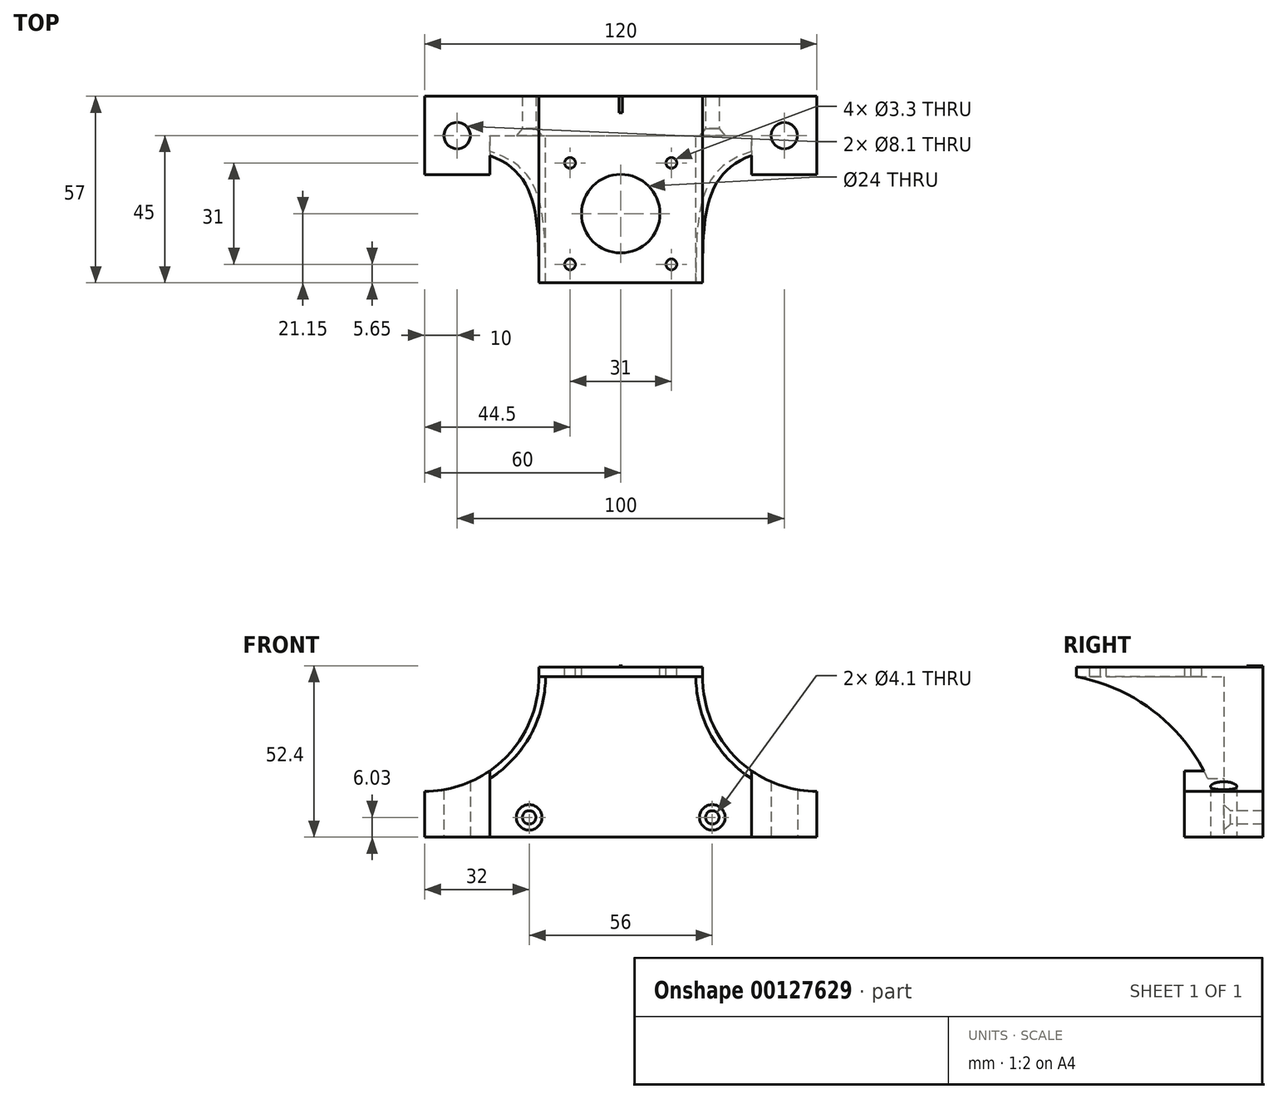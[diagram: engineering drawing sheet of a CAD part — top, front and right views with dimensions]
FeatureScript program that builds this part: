
annotation { "Feature Type Name" : "Feature", "Feature Type Description" : "" }
export const myFeature = defineFeature(function(context is Context, id is Id, definition is map)
    precondition{}
    {
        {
            var Q0;
            Q0=qCreatedBy(makeId("Front.planeOp"),FACE);
            var sketch = newSketch(context, id + "F0", { "sketchPlane" : qUnion([Q0])});
            skLineSegment(sketch, "E0.bottom", {"start": v(-27.18, 22.72) * mm, "end": v(22.82, 22.72) * mm});
            skLineSegment(sketch, "E0.top", {"start": v(-62.18, -29.28) * mm, "end": v(57.82, -29.28) * mm});
            skLineSegment(sketch, "E0.right", {"start": v(57.82, -15.28) * mm, "end": v(57.82, -29.28) * mm});
            skPoint(sketch, "E1", {"position": v(-2.18, 22.72) * mm});
            skLineSegment(sketch, "E2.top", {"start": v(-27.18, 19.72) * mm, "end": v(22.82, 19.72) * mm});
            skLineSegment(sketch, "E2.left", {"start": v(-27.18, 22.72) * mm, "end": v(-27.18, 19.72) * mm});
            skLineSegment(sketch, "E2.right", {"start": v(22.82, 22.72) * mm, "end": v(22.82, 19.72) * mm});
            skLineSegment(sketch, "E3", {"start": v(-62.18, -15.28) * mm, "end": v(57.82, -15.28) * mm, "construction": true});
            skArc(sketch, "E4", {"start": v(-62.18, -15.28) * mm, "mid": v(-37.43, -5.03) * mm, "end": v(-27.18, 19.72) * mm});
            skArc(sketch, "E5", {"start": v(22.82, 19.72) * mm, "mid": v(33.07, -5.03) * mm, "end": v(57.82, -15.28) * mm});
            skLineSegment(sketch, "E6.trimOffspring", {"start": v(-62.18, -15.28) * mm, "end": v(-62.18, -29.28) * mm});
            skPoint(sketch, "E0.left.start.orphan", {"position": v(-62.18, 22.72) * mm});
            skPoint(sketch, "E7.orphan", {"position": v(57.82, 22.72) * mm});
            skSolve(sketch);
        }
        {
            var Q0;
            Q0=makeQuery(id+"F0.imprint","IMPRINT",FACE,{"disambiguationData":[TD([[makeQuery(id+"F0.imprint","IMPRINT",EDGE,{"derivedFrom":sQuery(id+"F0.wireOp",EDGE,"E0.top")}),1.0]])]});
            var Q1;
            Q1=makeQuery(id+"F0.imprint","IMPRINT",FACE,{"disambiguationData":[TD([[makeQuery(id+"F0.imprint","IMPRINT",EDGE,{"derivedFrom":sQuery(id+"F0.wireOp",EDGE,"E0.bottom")}),-1.0]])]});
            extrude(context, id + "F1", {"entities" : qUnion([Q0, Q1]), "depth" : 12 * mm});
        }
        {
            var Q0;
            Q0=makeQuery(id+"F1.opExtrude","CAP_FACE",FACE,{"disambiguationData":[OSD([sQuery(id+"F0.wireOp",EDGE,"E0.top"),sQuery(id+"F0.wireOp",EDGE,"E0.right"),sQuery(id+"F0.wireOp",EDGE,"E0.bottom"),sQuery(id+"F0.wireOp",EDGE,"E2.left"),sQuery(id+"F0.wireOp",EDGE,"E2.right"),sQuery(id+"F0.wireOp",EDGE,"E4"),sQuery(id+"F0.wireOp",EDGE,"E5"),sQuery(id+"F0.wireOp",EDGE,"E6.trimOffspring")])],"isStart":false});
            var sketch = newSketch(context, id + "F2", { "sketchPlane" : qUnion([Q0])});
            skLineSegment(sketch, "E8", {"start": v(-27.18, 19.72) * mm, "end": v(22.82, 19.72) * mm});
            skArc(sketch, "E9.0", {"start": v(-60.18, -17.22) * mm, "mid": v(-35.32, -5.72) * mm, "end": v(-25.18, 19.72) * mm});
            skArc(sketch, "E10.0", {"start": v(20.82, 19.72) * mm, "mid": v(30.96, -5.72) * mm, "end": v(55.82, -17.22) * mm});
            skLineSegment(sketch, "E11.0", {"start": v(-60.18, -17.22) * mm, "end": v(-60.18, -29.28) * mm});
            skLineSegment(sketch, "E12.0", {"start": v(55.82, -17.22) * mm, "end": v(55.82, -29.28) * mm});
            skSolve(sketch);
        }
        {
            var Q0;
            Q0=qSketchRegion(id+"F2",true);
            var Q1;
            {var subQ2=sQuery(id+"F2.wireOp",EDGE,"E9.0");Q1=makeQuery(id+"F2.imprint","IMPRINT",FACE,{"disambiguationData":[TD([[makeQuery(id+"F2.imprint","IMPRINT",EDGE,{"derivedFrom":subQ2}),1.0]])]});}
            var Q2;
            Q2=makeQuery(id+"F2.imprint","IMPRINT",FACE,{"disambiguationData":[TD([[makeQuery(id+"F2.imprint","IMPRINT",EDGE,{"derivedFrom":makeQuery(id+"F1.opExtrude","CAP_EDGE",EDGE,{"disambiguationData":[OSD([sQuery(id+"F0.wireOp",EDGE,"E0.bottom")])],"isStart":false})}),-1.0]])]});
            var Q3;
            {var subQ2=sQuery(id+"F2.wireOp",EDGE,"E10.0");Q3=makeQuery(id+"F2.imprint","IMPRINT",FACE,{"disambiguationData":[TD([[makeQuery(id+"F2.imprint","IMPRINT",EDGE,{"derivedFrom":subQ2}),1.0]])]});}
            extrude(context, id + "F3", {"entities" : qUnion([Q0, Q1, Q2, Q3]), "operationType" : NewBodyOperationType.ADD, "depth" : 45 * mm});
        }
        {
            var Q0;
            {var subQ0=sQuery(id+"F0.wireOp",EDGE,"E6.trimOffspring");Q0=makeQuery(id+"F3.boolean.opBoolean","MERGE",FACE,{"derivedFrom":[makeQuery(id+"F1.opExtrude","SWEPT_FACE",FACE,{"disambiguationData":[OSD([subQ0])]}),makeQuery(id+"F3.opExtrude","SWEPT_FACE",FACE,{"disambiguationData":[OSD([subQ0])]})]});}
            var sketch = newSketch(context, id + "F4", { "sketchPlane" : qUnion([Q0])});
            skPoint(sketch, "E13.0", {"position": v(57, 19.72) * mm});
            skPoint(sketch, "E14.0", {"position": v(12, -29.28) * mm});
            skArc(sketch, "E15", {"start": v(57, 19.72) * mm, "mid": v(26.33, 2.73) * mm, "end": v(12, -29.28) * mm});
            skLineSegment(sketch, "E16.0", {"start": v(57, -15.28) * mm, "end": v(57, 19.72) * mm});
            skLineSegment(sketch, "E17.0", {"start": v(57, -15.28) * mm, "end": v(57, -29.28) * mm});
            skLineSegment(sketch, "E18.0", {"start": v(57, -29.28) * mm, "end": v(0, -29.28) * mm});
            skSolve(sketch);
        }
        {
            var Q0;
            Q0=qSketchRegion(id+"F4",true);
            extrude(context, id + "F5", {"entities" : qUnion([Q0]), "operationType" : NewBodyOperationType.REMOVE, "endBound" : BoundingType.THROUGH_ALL, "oppositeDirection" : true, "depth" : 25 * mm});
        }
        {
            var Q0;
            {var subQ0=sQuery(id+"F0.wireOp",EDGE,"E0.bottom");Q0=makeQuery(id+"F3.boolean.opBoolean","MERGE",FACE,{"derivedFrom":[makeQuery(id+"F1.opExtrude","SWEPT_FACE",FACE,{"disambiguationData":[OSD([subQ0])]}),makeQuery(id+"F3.opExtrude","SWEPT_FACE",FACE,{"disambiguationData":[OSD([subQ0])]})]});}
            var sketch = newSketch(context, id + "F6", { "sketchPlane" : qUnion([Q0])});
            skLineSegment(sketch, "E19", {"start": v(-2.18, -57) * mm, "end": v(-2.18, 0) * mm, "construction": true});
            skLineSegment(sketch, "E20", {"start": v(-27.18, -35.85) * mm, "end": v(22.82, -35.85) * mm, "construction": true});
            skCircle(sketch, "E21", {"center": v(-2.18, -35.85) * mm, "radius": 12 * mm});
            skLineSegment(sketch, "E22", {"start": v(-27.18, -51.35) * mm, "end": v(22.82, -51.35) * mm, "construction": true});
            skLineSegment(sketch, "E23", {"start": v(-17.68, 0) * mm, "end": v(-17.68, -57) * mm, "construction": true});
            skCircle(sketch, "E24", {"center": v(-17.68, -51.35) * mm, "radius": 1.65 * mm});
            skCircle(sketch, "E25.0.1.0", {"center": v(-17.68, -20.35) * mm, "radius": 1.65 * mm});
            skCircle(sketch, "E25.1.0.0", {"center": v(13.32, -51.35) * mm, "radius": 1.65 * mm});
            skCircle(sketch, "E25.1.1.0", {"center": v(13.32, -20.35) * mm, "radius": 1.65 * mm});
            skLineSegment(sketch, "E25.direction1", {"start": v(-17.68, -51.35) * mm, "end": v(13.32, -51.35) * mm, "construction": true});
            skLineSegment(sketch, "E25.direction2", {"start": v(-17.68, -51.35) * mm, "end": v(-17.68, -20.35) * mm, "construction": true});
            skSolve(sketch);
        }
        {
            var Q0;
            Q0=qSketchRegion(id+"F6",true);
            extrude(context, id + "F7", {"entities" : qUnion([Q0]), "operationType" : NewBodyOperationType.REMOVE, "oppositeDirection" : true, "depth" : 25 * mm});
        }
        {
            var Q0;
            Q0=makeQuery(id+"F1.opExtrude","CAP_FACE",FACE,{"disambiguationData":[OSD([sQuery(id+"F0.wireOp",EDGE,"E0.top"),sQuery(id+"F0.wireOp",EDGE,"E0.right"),sQuery(id+"F0.wireOp",EDGE,"E0.bottom"),sQuery(id+"F0.wireOp",EDGE,"E2.left"),sQuery(id+"F0.wireOp",EDGE,"E2.right"),sQuery(id+"F0.wireOp",EDGE,"E4"),sQuery(id+"F0.wireOp",EDGE,"E5"),sQuery(id+"F0.wireOp",EDGE,"E6.trimOffspring")])],"isStart":false});
            var sketch = newSketch(context, id + "F8", { "sketchPlane" : qUnion([Q0])});
            skLineSegment(sketch, "E26", {"start": v(-60.18, -23.25) * mm, "end": v(55.82, -23.25) * mm, "construction": true});
            skLineSegment(sketch, "E27", {"start": v(-30.18, -23.25) * mm, "end": v(-30.18, -29.28) * mm, "construction": true});
            skLineSegment(sketch, "E28", {"start": v(25.82, -23.25) * mm, "end": v(25.82, -29.28) * mm, "construction": true});
            skPoint(sketch, "E29", {"position": v(-30.18, -23.25) * mm});
            skPoint(sketch, "E30", {"position": v(25.82, -23.25) * mm});
            skSolve(sketch);
        }
        {
            var Q0;
            Q0=sQuery(id+"F8.wireOp",VERTEX,"E29");
            var Q1;
            Q1=sQuery(id+"F8.wireOp",VERTEX,"E30");
            var Q2;
            Q2=makeQuery(id+"F1.opExtrude","SWEPT_BODY",BODY,{"disambiguationData":[OSD([sQuery(id+"F0.wireOp",EDGE,"E0.top"),sQuery(id+"F0.wireOp",EDGE,"E0.right"),sQuery(id+"F0.wireOp",EDGE,"E0.bottom"),sQuery(id+"F0.wireOp",EDGE,"E2.left"),sQuery(id+"F0.wireOp",EDGE,"E2.right"),sQuery(id+"F0.wireOp",EDGE,"E4"),sQuery(id+"F0.wireOp",EDGE,"E5"),sQuery(id+"F0.wireOp",EDGE,"E6.trimOffspring")])]});
            hole(context, id + "F9", {"style" : HoleStyle.C_SINK, "endStyle" : HoleEndStyle.THROUGH, "holeDiameter" : 4.1 * mm, "cSinkDiameter" : 7.8 * mm, "cSinkAngle" : 82 * degree, "locations" : qUnion([Q0, Q1]), "scope" : qUnion([Q2]), "isTappedThrough" : true});
        }
        {
            var Q0;
            {var subQ0=sQuery(id+"F0.wireOp",EDGE,"E0.bottom");Q0=makeQuery(id+"F3.boolean.opBoolean","MERGE",FACE,{"derivedFrom":[makeQuery(id+"F1.opExtrude","SWEPT_FACE",FACE,{"disambiguationData":[OSD([subQ0])]}),makeQuery(id+"F3.opExtrude","SWEPT_FACE",FACE,{"disambiguationData":[OSD([subQ0])]})]});}
            var sketch = newSketch(context, id + "F10", { "sketchPlane" : qUnion([Q0])});
            skPoint(sketch, "E31", {"position": v(-2.18, 0) * mm});
            skLineSegment(sketch, "E32.bottom", {"start": v(-2.68, -5) * mm, "end": v(-1.68, -5) * mm});
            skLineSegment(sketch, "E32.top", {"start": v(-2.68, 0) * mm, "end": v(-1.68, 0) * mm});
            skLineSegment(sketch, "E32.left", {"start": v(-2.68, -5) * mm, "end": v(-2.68, 0) * mm});
            skLineSegment(sketch, "E32.right", {"start": v(-1.68, -5) * mm, "end": v(-1.68, 0) * mm});
            skPoint(sketch, "E33", {"position": v(-2.18, -5) * mm});
            skSolve(sketch);
        }
        {
            var Q0;
            Q0=qSketchRegion(id+"F10",true);
            extrude(context, id + "F11", {"entities" : qUnion([Q0]), "operationType" : NewBodyOperationType.ADD, "depth" : 0.4 * mm});
        }
        {
            var Q0;
            {var subQ0=sQuery(id+"F0.wireOp",EDGE,"E0.top");var subQ1=makeQuery(id+"F1.opExtrude","CAP_EDGE",EDGE,{"disambiguationData":[OSD([subQ0])],"isStart":false});Q0=makeQuery(id+"F3.boolean.opBoolean","MERGE",FACE,{"derivedFrom":[makeQuery(id+"F1.opExtrude","SWEPT_FACE",FACE,{"disambiguationData":[OSD([subQ0])]}),makeQuery(id+"F3.opExtrude","SWEPT_FACE",FACE,{"disambiguationData":[OSD([subQ0]),TDD([makeQuery(id+"F2.imprint","IMPRINT",EDGE,{"disambiguationData":[TD([[makeQuery(id+"F2.imprint","INTERSECT",VERTEX,{"derivedFrom":[subQ1,makeQuery(id+"F1.opExtrude","CAP_EDGE",EDGE,{"disambiguationData":[OSD([sQuery(id+"F0.wireOp",EDGE,"E6.trimOffspring")])],"isStart":false})]}),-1.0]])],"derivedFrom":subQ1})])]}),makeQuery(id+"F3.opExtrude","SWEPT_FACE",FACE,{"disambiguationData":[OSD([subQ0]),TDD([makeQuery(id+"F2.imprint","IMPRINT",EDGE,{"disambiguationData":[TD([[makeQuery(id+"F2.imprint","INTERSECT",VERTEX,{"derivedFrom":[subQ1,makeQuery(id+"F1.opExtrude","CAP_EDGE",EDGE,{"disambiguationData":[OSD([sQuery(id+"F0.wireOp",EDGE,"E0.right")])],"isStart":false})]}),1.0]])],"derivedFrom":subQ1})])]})]});}
            var sketch = newSketch(context, id + "F12", { "sketchPlane" : qUnion([Q0])});
            skLineSegment(sketch, "E34", {"start": v(-52.18, 0) * mm, "end": v(-52.18, 12) * mm, "construction": true});
            skLineSegment(sketch, "E35", {"start": v(47.82, 0) * mm, "end": v(47.82, 12) * mm, "construction": true});
            skLineSegment(sketch, "E36.bottom", {"start": v(-62.18, 0) * mm, "end": v(-42.18, 0) * mm});
            skLineSegment(sketch, "E36.top", {"start": v(-62.18, 24) * mm, "end": v(-42.18, 24) * mm});
            skLineSegment(sketch, "E36.left", {"start": v(-62.18, 0) * mm, "end": v(-62.18, 24) * mm});
            skLineSegment(sketch, "E36.right", {"start": v(-42.18, 0) * mm, "end": v(-42.18, 24) * mm});
            skCircle(sketch, "E37", {"center": v(-52.18, 12) * mm, "radius": 4.05 * mm});
            skLineSegment(sketch, "E38.bottom", {"start": v(57.82, 0) * mm, "end": v(37.82, 0) * mm});
            skLineSegment(sketch, "E38.top", {"start": v(57.82, 24) * mm, "end": v(37.82, 24) * mm});
            skLineSegment(sketch, "E38.left", {"start": v(57.82, 0) * mm, "end": v(57.82, 24) * mm});
            skLineSegment(sketch, "E38.right", {"start": v(37.82, 0) * mm, "end": v(37.82, 24) * mm});
            skCircle(sketch, "E39", {"center": v(47.82, 12) * mm, "radius": 4.05 * mm});
            skSolve(sketch);
        }
        {
            var Q0;
            {var subQ6=sQuery(id+"F12.wireOp",EDGE,"E36.top");Q0=makeQuery(id+"F12.imprint","IMPRINT",FACE,{"disambiguationData":[TD([[makeQuery(id+"F12.imprint","IMPRINT",EDGE,{"derivedFrom":subQ6}),-1.0]])]});}
            var Q1;
            {var subQ0=sQuery(id+"F12.wireOp",EDGE,"E37");var subQ1=makeQuery(id+"F1.opExtrude","CAP_EDGE",EDGE,{"disambiguationData":[OSD([sQuery(id+"F0.wireOp",EDGE,"E0.top")])],"isStart":false});var subQ2=makeQuery(id+"F12.imprint","INTERSECT",VERTEX,{"disambiguationData":[OD(0.0)],"derivedFrom":[subQ1,subQ0]});Q1=makeQuery(id+"F12.imprint","IMPRINT",FACE,{"disambiguationData":[TD([[makeQuery(id+"F12.imprint","IMPRINT",EDGE,{"disambiguationData":[TD([[subQ2,1.0]])],"derivedFrom":subQ0}),1.0]])]});}
            var Q2;
            {var subQ0=sQuery(id+"F0.wireOp",EDGE,"E4");Q2=makeQuery(id+"F3.boolean.opBoolean","MERGE",FACE,{"derivedFrom":[makeQuery(id+"F1.opExtrude","SWEPT_FACE",FACE,{"disambiguationData":[OSD([subQ0])]}),makeQuery(id+"F3.opExtrude","SWEPT_FACE",FACE,{"disambiguationData":[OSD([subQ0])]})]});}
            extrude(context, id + "F13", {"entities" : qUnion([Q0, Q1]), "operationType" : NewBodyOperationType.ADD, "endBound" : BoundingType.UP_TO_SURFACE, "oppositeDirection" : true, "endBoundEntityFace" : qUnion([Q2]), "depth" : 25 * mm});
        }
        {
            var Q0;
            {var subQ6=sQuery(id+"F12.wireOp",EDGE,"E38.top");Q0=makeQuery(id+"F12.imprint","IMPRINT",FACE,{"disambiguationData":[TD([[makeQuery(id+"F12.imprint","IMPRINT",EDGE,{"derivedFrom":subQ6}),1.0]])]});}
            var Q1;
            {var subQ0=sQuery(id+"F12.wireOp",EDGE,"E39");var subQ1=makeQuery(id+"F1.opExtrude","CAP_EDGE",EDGE,{"disambiguationData":[OSD([sQuery(id+"F0.wireOp",EDGE,"E0.top")])],"isStart":false});var subQ2=makeQuery(id+"F12.imprint","INTERSECT",VERTEX,{"disambiguationData":[OD(0.0)],"derivedFrom":[subQ1,subQ0]});Q1=makeQuery(id+"F12.imprint","IMPRINT",FACE,{"disambiguationData":[TD([[makeQuery(id+"F12.imprint","IMPRINT",EDGE,{"disambiguationData":[TD([[subQ2,-1.0]])],"derivedFrom":subQ0}),1.0]])]});}
            var Q2;
            {var subQ0=sQuery(id+"F0.wireOp",EDGE,"E5");Q2=makeQuery(id+"F3.boolean.opBoolean","MERGE",FACE,{"derivedFrom":[makeQuery(id+"F1.opExtrude","SWEPT_FACE",FACE,{"disambiguationData":[OSD([subQ0])]}),makeQuery(id+"F3.opExtrude","SWEPT_FACE",FACE,{"disambiguationData":[OSD([subQ0])]})]});}
            extrude(context, id + "F14", {"entities" : qUnion([Q0, Q1]), "operationType" : NewBodyOperationType.ADD, "endBound" : BoundingType.UP_TO_SURFACE, "oppositeDirection" : true, "endBoundEntityFace" : qUnion([Q2]), "depth" : 25 * mm});
        }
        {
            var Q0;
            {var subQ0=sQuery(id+"F12.wireOp",EDGE,"E37");var subQ1=makeQuery(id+"F1.opExtrude","CAP_EDGE",EDGE,{"disambiguationData":[OSD([sQuery(id+"F0.wireOp",EDGE,"E0.top")])],"isStart":false});var subQ2=makeQuery(id+"F12.imprint","INTERSECT",VERTEX,{"disambiguationData":[OD(0.0)],"derivedFrom":[subQ1,subQ0]});Q0=makeQuery(id+"F12.imprint","IMPRINT",FACE,{"disambiguationData":[TD([[makeQuery(id+"F12.imprint","IMPRINT",EDGE,{"disambiguationData":[TD([[subQ2,1.0]])],"derivedFrom":subQ0}),1.0]])]});}
            var Q1;
            {var subQ0=sQuery(id+"F12.wireOp",EDGE,"E37");var subQ1=makeQuery(id+"F1.opExtrude","CAP_EDGE",EDGE,{"disambiguationData":[OSD([sQuery(id+"F0.wireOp",EDGE,"E0.top")])],"isStart":false});var subQ2=makeQuery(id+"F12.imprint","INTERSECT",VERTEX,{"disambiguationData":[OD(0.0)],"derivedFrom":[subQ1,subQ0]});Q1=makeQuery(id+"F12.imprint","IMPRINT",FACE,{"disambiguationData":[TD([[makeQuery(id+"F12.imprint","IMPRINT",EDGE,{"disambiguationData":[TD([[subQ2,-1.0]])],"derivedFrom":subQ0}),1.0]])]});}
            var Q2;
            {var subQ0=sQuery(id+"F12.wireOp",EDGE,"E39");var subQ1=makeQuery(id+"F1.opExtrude","CAP_EDGE",EDGE,{"disambiguationData":[OSD([sQuery(id+"F0.wireOp",EDGE,"E0.top")])],"isStart":false});var subQ2=makeQuery(id+"F12.imprint","INTERSECT",VERTEX,{"disambiguationData":[OD(0.0)],"derivedFrom":[subQ1,subQ0]});Q2=makeQuery(id+"F12.imprint","IMPRINT",FACE,{"disambiguationData":[TD([[makeQuery(id+"F12.imprint","IMPRINT",EDGE,{"disambiguationData":[TD([[subQ2,-1.0]])],"derivedFrom":subQ0}),1.0]])]});}
            var Q3;
            {var subQ0=sQuery(id+"F12.wireOp",EDGE,"E39");var subQ1=makeQuery(id+"F1.opExtrude","CAP_EDGE",EDGE,{"disambiguationData":[OSD([sQuery(id+"F0.wireOp",EDGE,"E0.top")])],"isStart":false});var subQ2=makeQuery(id+"F12.imprint","INTERSECT",VERTEX,{"disambiguationData":[OD(0.0)],"derivedFrom":[subQ1,subQ0]});Q3=makeQuery(id+"F12.imprint","IMPRINT",FACE,{"disambiguationData":[TD([[makeQuery(id+"F12.imprint","IMPRINT",EDGE,{"disambiguationData":[TD([[subQ2,1.0]])],"derivedFrom":subQ0}),1.0]])]});}
            extrude(context, id + "F15", {"entities" : qUnion([Q0, Q1, Q2, Q3]), "operationType" : NewBodyOperationType.REMOVE, "oppositeDirection" : true, "depth" : 25 * mm});
        }
    });
